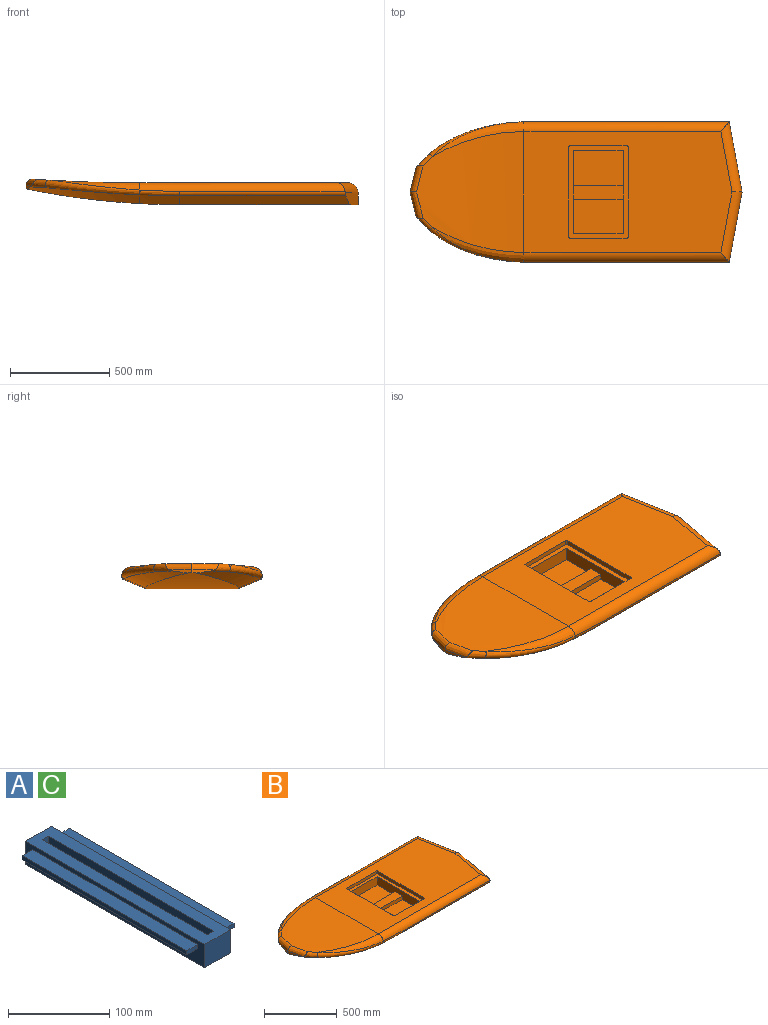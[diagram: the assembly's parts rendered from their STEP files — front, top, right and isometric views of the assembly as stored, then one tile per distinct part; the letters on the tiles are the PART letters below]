
ASSEMBLY  parts=3 mates=2
PART A: 25 faces, bbox 66x250x28 mm
  f0: plane 15x5mm, normal (0,1,0), area 75mm2, adj f15,f16,f17,f18
  f1: plane 15x5mm, normal (0,-1,0), area 75mm2, adj f15,f16,f17,f18
  f2: plane 230x10mm, normal (-1,0,0), area 2300mm2, adj f3,f9,f21,f24
  f3: plane 230x4mm, normal (0,0,-1), area 920mm2, adj f2,f4,f21,f24
  f4: plane 230x8mm, normal (-1,0,0), area 1840mm2, adj f3,f5,f21,f24
  f5: plane 230x17mm, normal (0,0,1), area 3910mm2, adj f4,f6,f21,f24
  f6: plane 230x8mm, normal (1,0,0), area 1840mm2, adj f5,f7,f21,f24
  f7: plane 230x4mm, normal (0,0,-1), area 920mm2, adj f6,f8,f21,f24
  f8: plane 230x10mm, normal (1,0,0), area 2300mm2, adj f7,f9,f21,f24
  f9: plane 250x36mm, normal (0,0,1), area 6930mm2, adj f2,f8,f13,f15,f21,f22,f23,f24
  f10: plane 230x15mm, normal (0,0,1), area 3450mm2, adj f11,f13,f19,f20
  f11: plane 230x5mm, normal (-1,0,0), area 1150mm2, adj f10,f12,f19,f20
  f12: plane 230x15mm, normal (0,0,-1), area 3450mm2, adj f11,f13,f19,f20
  f13: plane 250x28mm, normal (-1,0,0), area 5850mm2, adj f9,f10,f12,f14,f19,f20,f22,f23
  f14: plane 250x36mm, normal (0,0,-1), area 9000mm2, adj f13,f15,f22,f23
  f15: plane 250x28mm, normal (1,0,0), area 5850mm2, adj f0,f1,f9,f14,f16,f18,f22,f23
  f16: plane 230x15mm, normal (0,0,-1), area 3450mm2, adj f0,f1,f15,f17
  f17: plane 230x5mm, normal (1,0,0), area 1150mm2, adj f0,f1,f16,f18
  f18: plane 230x15mm, normal (0,0,1), area 3450mm2, adj f0,f1,f15,f17
  f19: plane 15x5mm, normal (0,-1,0), area 75mm2, adj f10,f11,f12,f13
  f20: plane 15x5mm, normal (0,1,0), area 75mm2, adj f10,f11,f12,f13
  f21: plane 18x17mm, normal (0,1,0), area 226mm2, adj f2,f3,f4,f5,f6,f7,f8,f9
  f22: plane 36x28mm, normal (0,-1,0), area 1008mm2, adj f9,f13,f14,f15
  f23: plane 36x28mm, normal (0,1,0), area 1008mm2, adj f9,f13,f14,f15
  f24: plane 18x17mm, normal (0,-1,0), area 226mm2, adj f2,f3,f4,f5,f6,f7,f8,f9
PART B: 50 faces, bbox 1764.4x717.7x134.6 mm
  f0: plane 250x173.94mm, normal (0,0,1), area 43484.3mm2, adj f1,f40,f42,f43
  f1: plane 415x70mm, normal (1,0,0), area 26950mm2, adj f0,f38,f39,f41,f42,f43,f44,f45
  f2: plane 1049.17x610mm, normal (0,0,1), area 483481.7mm2, adj f9,f19,f20,f21,f23,f34,f35,f36
  f3: plane 117.75x29.97mm, normal (-0.97,-0.24,0), area 1532.9mm2, adj f4,f8,f11,f14,f24
  f4: plane 117.82x30.05mm, normal (-0.97,0.24,0), area 1533mm2, adj f3,f8,f10,f17,f33
  f5: plane 355.28x65.64mm, normal (0.98,-0.18,0), area 18570.7mm2, adj f6,f7,f12,f21,f28
  f6: plane 355.28x65.64mm, normal (0.98,0.18,0), area 18570.7mm2, adj f5,f7,f15,f20,f29
  f7: plane 900x470mm, normal (0,0,-1), area 412888.4mm2, adj f5,f6,f8,f12,f15
  f8: cylinder r=3793.91mm len=775mm, axis (0,1,0), area 287897.1mm2, adj f3,f4,f7,f13,f14,f16,f17
  f9: cylinder r=8275.62mm len=610mm, axis (0,1,0), area 242497.9mm2, adj f2,f10,f11,f18,f22,f24,f33
  f10: bspline ~145.91x65.61mm, area 6274.9mm2, adj f4,f9,f11,f33
  f11: bspline ~145.91x65.61mm, area 6274.9mm2, adj f3,f9,f10,f24
  f12: plane 856.97x107.51mm, normal (0,-0.38,-0.92), area 98668.7mm2, adj f5,f7,f13,f28
  f13: cone r=3743.91mm half-angle=22.6deg, axis (0,1,0), area 23373.3mm2, adj f8,f12,f14,f27
  f14: bspline ~629.92x317.13mm, area 58560.1mm2, adj f3,f8,f13,f24,f25,f26
  f15: plane 856.97x107.51mm, normal (0,0.38,-0.92), area 98668.7mm2, adj f6,f7,f16,f29
  f16: cone r=3793.91mm half-angle=22.6deg, axis (0,-1,0), area 23373.5mm2, adj f8,f15,f17,f30
  f17: bspline ~663.59x351.02mm, area 58560.1mm2, adj f4,f8,f16,f31,f32,f33
  f18: bspline ~567.57x191.28mm, area 15823.2mm2, adj f9,f19,f32
  f19: cylinder r=50mm len=1034.75mm, axis (-1,0,0), area 73900.2mm2, adj f2,f18,f20,f29,f30,f31
  f20: cylinder r=50mm len=363.76mm, axis (0.18,-0.98,0), area 26794.7mm2, adj f2,f6,f19,f21,f29
  f21: cylinder r=50mm len=363.76mm, axis (-0.18,-0.98,0), area 26794.7mm2, adj f2,f5,f20,f23,f28
  f22: bspline ~528.67x184.48mm, area 15813.5mm2, adj f9,f23,f25
  f23: cylinder r=50mm len=1034.75mm, axis (-1,0,0), area 73900.2mm2, adj f2,f21,f22,f26,f27,f28
  f24: bspline ~205.06x204.73mm, area 5025.1mm2, adj f3,f9,f11,f14,f25
  f25: bspline ~538.65x181.66mm, area 20095.9mm2, adj f14,f22,f24,f26
  f26: bspline ~47.25x27.46mm, area 16.2mm2, adj f14,f23,f25,f27
  f27: bspline ~261.83x32.31mm, area 5367.1mm2, adj f13,f23,f26,f28
  f28: cylinder r=20mm len=837.29mm, axis (-1,0,0), area 21480.8mm2, adj f5,f12,f21,f23,f27
  f29: cylinder r=20mm len=837.29mm, axis (-1,0,0), area 21480.8mm2, adj f6,f15,f19,f20,f30
  f30: bspline ~261.83x32.31mm, area 5367.1mm2, adj f16,f19,f29,f31
  f31: bspline ~47.25x27.46mm, area 16.9mm2, adj f17,f19,f30,f32
  f32: bspline ~540.03x181.78mm, area 20095.8mm2, adj f17,f18,f31,f33
  f33: bspline ~205.06x204.73mm, area 5025.1mm2, adj f4,f9,f10,f17,f32
  f34: plane 290x25mm, normal (0,-1,0), area 7250mm2, adj f2,f38,f46,f49
  f35: plane 455x25mm, normal (1,0,0), area 11375mm2, adj f2,f38,f46,f47
  f36: plane 290x25mm, normal (0,1,0), area 7250mm2, adj f2,f38,f47,f48
  f37: plane 455x25mm, normal (-1,0,0), area 11375mm2, adj f2,f38,f48,f49
  f38: plane 465x300mm, normal (0,0,1), area 35728.5mm2, adj f1,f34,f35,f36,f37,f40,f41,f42
  f39: plane 250x171.06mm, normal (0,0,1), area 42765.7mm2, adj f1,f40,f41,f44
  f40: plane 415x70mm, normal (-1,0,0), area 26950mm2, adj f0,f38,f39,f41,f42,f43,f44,f45
  f41: plane 250x70mm, normal (0,1,0), area 17500mm2, adj f1,f38,f39,f40
  f42: plane 250x70mm, normal (0,-1,0), area 17500mm2, adj f0,f1,f38,f40
  f43: plane 250x30mm, normal (0,1,0), area 7500mm2, adj f0,f1,f40,f45
  f44: plane 250x30mm, normal (0,-1,0), area 7500mm2, adj f1,f39,f40,f45
  f45: plane 250x70mm, normal (0,0,1), area 17500mm2, adj f1,f40,f43,f44
  f46: cylinder r=5mm len=25mm, axis (0,0,1), area 196.3mm2, adj f2,f34,f35,f38
  f47: cylinder r=5mm len=25mm, axis (0,0,-1), area 196.3mm2, adj f2,f35,f36,f38
  f48: cylinder r=5mm len=25mm, axis (0,0,1), area 196.3mm2, adj f2,f36,f37,f38
  f49: cylinder r=5mm len=25mm, axis (0,0,-1), area 196.3mm2, adj f2,f34,f37,f38
PART C: same geometry as A
PLACE A rot(axis=(-0.71,-0.71,0),180deg) t=(245.86,-334.83,56.95)mm
PLACE B rot(axis=(1,0,0),0deg) t=(-317.99,181.85,28.95)mm
PLACE C rot(axis=(-0.71,-0.71,0),180deg) t=(252.85,-155.22,56.95)mm
MATE planar B.f7 <-> A.f9  axis (0,0,-1) through (-113.3,-173.15,28.95)mm
MATE planar B.f7 <-> C.f9  axis (0,0,-1) through (-113.3,-173.15,28.95)mm
